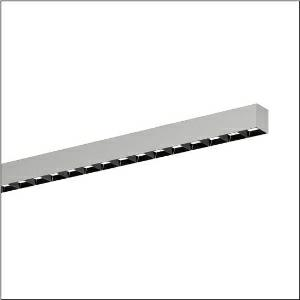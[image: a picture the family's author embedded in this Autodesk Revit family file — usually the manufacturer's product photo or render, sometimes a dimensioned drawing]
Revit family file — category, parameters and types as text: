
# Revit family: silica_21_51mx21tat4s
name_source: partatom
category: Lighting Fixtures
units: mm (PartAtom-declared; Revit-internal decimal feet)

## family parameters
Cut with Voids When Loaded = No
Host = Face
Light Source = No
Part Type = Normal
Room Calculation Point = No
Round Connector Dimension = Use Diameter
Shared = No

## types (1)
- --- (1 x LED, 3720 lm, 32.2 W, 6500K)
    Apparent Load = 32 VA
    CIE Flux Codes = 85 99 100 100 100
    Color Rendering = 80
    Color Temperature = 6500K
    Default Elevation = 1800 mm
    Description = Silica 21, office luminaire, primary light control with darklight reflector, of PMMA, black, CAT 2 (L<= 3000cd/m²), light emission: direct distribution, primary light characteristic: symmetric, installation type: surface-mounted, LED, rated luminous flux: 3.720lm, luminous efficacy: 110lm/W, light colour: 8tw, colour temperature: 2700..6500K, control gear: DALI DT8, with terminal, 3+2-pole, max. 2.5mm², mains connection: 220..240V, AC, 50/60Hz, rated input power: 33.8W, luminaire housing, of aluminium, metallic grey (RAL 9006), length: 1.204mm, width: 53mm, height: 53mm, protection rating (complete): IP20, insulation class (complete): insulation class I (protective earthing), certification: CE, permissible operating ambient temperature: 0..+35°C, standard: EN 50419, packaging unit: 1 piece
    Height = 53 mm
    Lamp = 1 x LED
    Lamp Light Flux = 3720 lm
    Lamp Power = 32.2 W
    Lamp count = 1
    Length = 1204 mm
    Luminous efficacy = 116 lm/W
    Manufacturer = Siteco
    ModVariant = No
    Model = 51MX21TAT4S
    Mounting Place = Ceiling
    Mounting Type = Surface mounted
    Number of Poles = 1
    OnlyDefault = Yes
    Power Factor = 1
    Product Name = Silica 21
    Product group = office luminaire | ceiling mounted
    ProductGroupID = 301
    Protection Class = Protection class I
    Protection Degree = IP 20
    RLX_Detail_Level = 1
    RLX_Emergency_Light_Flux = 0 lm
    RLX_Emergency_Type = 0
    RLX_Emergency_Type_DB = No
    RlxData = <blob elided: 39217 chars, md5=2f4a8933>
    Socket = socket
    Standby Power = 0 W
    System Light Flux = 3720 lm
    System Power = 32 W
    Type Comments = individual setting
    Type Image = l_1335929.jpg
    URL = http://relux.com
    VarID = @adj_139547
    Voltage = 0 V
    Weight = 0.00 kg
    Width = 53 mm

## geometry (parser evidence)
native form markers: Blend x4, Sweep x10
no freeform markers — native parametric forms only
